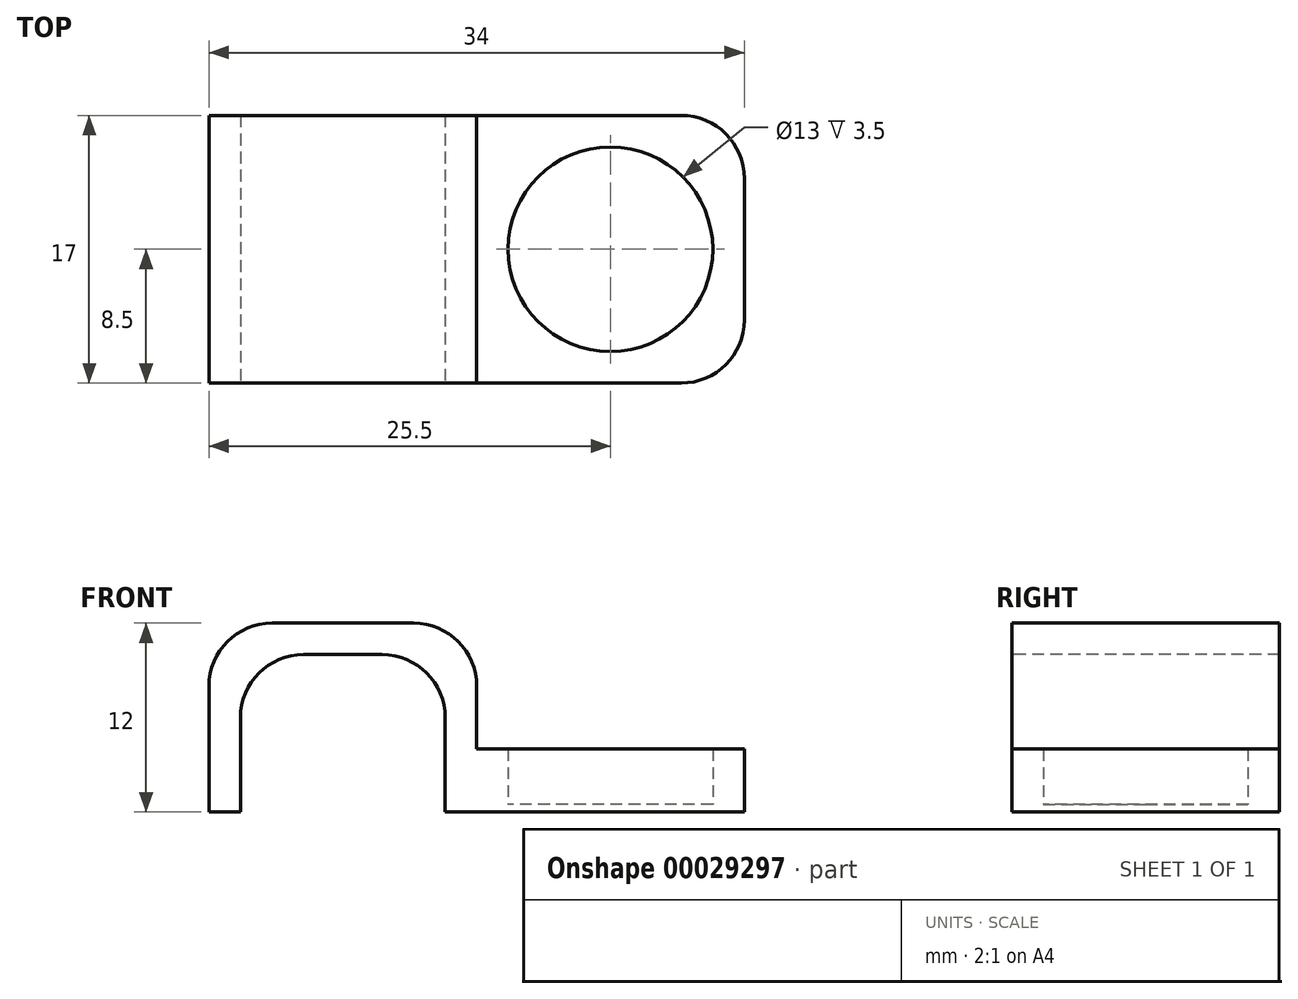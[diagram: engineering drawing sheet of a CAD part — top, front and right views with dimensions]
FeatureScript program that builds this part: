
annotation { "Feature Type Name" : "Feature", "Feature Type Description" : "" }
export const myFeature = defineFeature(function(context is Context, id is Id, definition is map)
    precondition{}
    {
        {
            var Q0;
            Q0=qCreatedBy(makeId("Top.planeOp"),FACE);
            var sketch = newSketch(context, id + "F0", { "sketchPlane" : qUnion([Q0])});
            skCircle(sketch, "E0", {"center": v(0, 0) * mm, "radius": 6.5 * mm});
            skLineSegment(sketch, "E1.rect.bottom", {"start": v(8.5, 8.5) * mm, "end": v(-8.5, 8.5) * mm});
            skLineSegment(sketch, "E1.rect.top", {"start": v(8.5, -8.5) * mm, "end": v(-8.5, -8.5) * mm});
            skLineSegment(sketch, "E1.rect.left", {"start": v(8.5, 8.5) * mm, "end": v(8.5, -8.5) * mm});
            skLineSegment(sketch, "E1.rect.right", {"start": v(-8.5, 8.5) * mm, "end": v(-8.5, -8.5) * mm});
            skLineSegment(sketch, "E2", {"start": v(-8.5, 8.5) * mm, "end": v(-25.5, 8.5) * mm});
            skLineSegment(sketch, "E3", {"start": v(-25.5, 8.5) * mm, "end": v(-25.5, -8.5) * mm});
            skLineSegment(sketch, "E4", {"start": v(-25.5, -8.5) * mm, "end": v(-8.5, -8.5) * mm});
            skSolve(sketch);
        }
        {
            var Q0;
            Q0=makeQuery(id+"F0.imprint","IMPRINT",FACE,{"disambiguationData":[TD([[makeQuery(id+"F0.imprint","IMPRINT",EDGE,{"derivedFrom":sQuery(id+"F0.wireOp",EDGE,"E0")}),-1.0]])]});
            extrude(context, id + "F1", {"entities" : qUnion([Q0]), "depth" : 4 * mm});
        }
        {
            var Q0;
            Q0=makeQuery(id+"F0.imprint","IMPRINT",FACE,{"disambiguationData":[TD([[makeQuery(id+"F0.imprint","IMPRINT",EDGE,{"derivedFrom":sQuery(id+"F0.wireOp",EDGE,"E0")}),1.0]])]});
            extrude(context, id + "F2", {"entities" : qUnion([Q0]), "operationType" : NewBodyOperationType.ADD, "depth" : .5 * mm});
        }
        {
            var Q0;
            Q0=makeQuery(id+"F0.imprint","IMPRINT",FACE,{"disambiguationData":[TD([[makeQuery(id+"F0.imprint","IMPRINT",EDGE,{"derivedFrom":sQuery(id+"F0.wireOp",EDGE,"E1.rect.right")}),-1.0]])]});
            extrude(context, id + "F3", {"entities" : qUnion([Q0]), "operationType" : NewBodyOperationType.ADD, "depth" : 12 * mm});
        }
        {
            var Q0;
            Q0=makeQuery(id+"F3.boolean.opBoolean","MERGE",FACE,{"derivedFrom":[makeQuery(id+"F1.opExtrude","SWEPT_FACE",FACE,{"disambiguationData":[OSD([sQuery(id+"F0.wireOp",EDGE,"E1.rect.top")])]}),makeQuery(id+"F3.opExtrude","SWEPT_FACE",FACE,{"disambiguationData":[OSD([sQuery(id+"F0.wireOp",EDGE,"E4")])]})]});
            var sketch = newSketch(context, id + "F4", { "sketchPlane" : qUnion([Q0])});
            skLineSegment(sketch, "E5.0", {"start": v(-25.5, 12) * mm, "end": v(-25.5, 0) * mm});
            skLineSegment(sketch, "E5.1", {"start": v(-25.5, 0) * mm, "end": v(-8.5, 0) * mm});
            skLineSegment(sketch, "E5.2", {"start": v(-8.5, 12) * mm, "end": v(-8.5, 4) * mm});
            skLineSegment(sketch, "E5.3", {"start": v(-25.5, 12) * mm, "end": v(-8.5, 12) * mm});
            skLineSegment(sketch, "E5.4", {"start": v(8.5, 0) * mm, "end": v(-8.5, 0) * mm});
            skLineSegment(sketch, "E5.5", {"start": v(8.5, 4) * mm, "end": v(-8.5, 4) * mm});
            skLineSegment(sketch, "E5.6", {"start": v(8.5, 4) * mm, "end": v(8.5, 0) * mm});
            skLineSegment(sketch, "E6", {"start": v(-23.5, 0) * mm, "end": v(-23.5, 10) * mm});
            skLineSegment(sketch, "E7", {"start": v(-23.5, 10) * mm, "end": v(-10.5, 10) * mm});
            skLineSegment(sketch, "E8", {"start": v(-10.5, 10) * mm, "end": v(-10.5, 0) * mm});
            skLineSegment(sketch, "E9", {"start": v(-17, 10) * mm, "end": v(-17, 12) * mm, "construction": true});
            skLineSegment(sketch, "E10", {"start": v(-23.5, 5) * mm, "end": v(-25.5, 5) * mm, "construction": true});
            skLineSegment(sketch, "E11", {"start": v(-10.5, 5) * mm, "end": v(-8.5, 5) * mm, "construction": true});
            skSolve(sketch);
        }
        {
            var Q0;
            {var subQ1=sQuery(id+"F4.wireOp",EDGE,"E6");Q0=makeQuery(id+"F4.imprint","IMPRINT",FACE,{"disambiguationData":[TD([[makeQuery(id+"F4.imprint","IMPRINT",EDGE,{"derivedFrom":subQ1}),-1.0]])]});}
            extrude(context, id + "F5", {"entities" : qUnion([Q0]), "operationType" : NewBodyOperationType.REMOVE, "endBound" : BoundingType.THROUGH_ALL, "oppositeDirection" : true, "depth" : 25 * mm});
        }
        {
            var Q0;
            Q0=makeQuery(id+"F5.boolean.opBoolean","COPY",EDGE,{"derivedFrom":makeQuery(id+"F5.opExtrude","SWEPT_EDGE",EDGE,{"disambiguationData":[OSD([sQuery(id+"F4.wireOp",EDGE,"E6"),sQuery(id+"F4.wireOp",EDGE,"E7")])]})});
            var Q1;
            Q1=makeQuery(id+"F5.boolean.opBoolean","COPY",EDGE,{"derivedFrom":makeQuery(id+"F5.opExtrude","SWEPT_EDGE",EDGE,{"disambiguationData":[OSD([sQuery(id+"F4.wireOp",EDGE,"E7"),sQuery(id+"F4.wireOp",EDGE,"E8")])]})});
            var Q2;
            Q2=makeQuery(id+"F3.opExtrude","CAP_EDGE",EDGE,{"disambiguationData":[OSD([sQuery(id+"F0.wireOp",EDGE,"E3")])],"isStart":false});
            var Q3;
            Q3=makeQuery(id+"F3.opExtrude","CAP_EDGE",EDGE,{"disambiguationData":[OSD([sQuery(id+"F0.wireOp",EDGE,"E1.rect.right")])],"isStart":false});
            var Q4;
            Q4=makeQuery(id+"F1.opExtrude","SWEPT_EDGE",EDGE,{"disambiguationData":[OSD([sQuery(id+"F0.wireOp",EDGE,"E1.rect.top"),sQuery(id+"F0.wireOp",EDGE,"E1.rect.left")])]});
            var Q5;
            Q5=makeQuery(id+"F1.opExtrude","SWEPT_EDGE",EDGE,{"disambiguationData":[OSD([sQuery(id+"F0.wireOp",EDGE,"E1.rect.bottom"),sQuery(id+"F0.wireOp",EDGE,"E1.rect.left")])]});
            var Q6;
            Q6=makeQuery(id+"F1.opExtrude","CAP_EDGE",EDGE,{"disambiguationData":[OSD([sQuery(id+"F0.wireOp",EDGE,"E1.rect.right")])],"isStart":false});
            fillet(context, id + "F6", {"entities" : qUnion([Q0, Q1, Q2, Q3, Q4, Q5, Q6]), "radius" : 4 * mm, "tangentPropagation" : true, "allowEdgeOverflow" : false});
        }
    });
